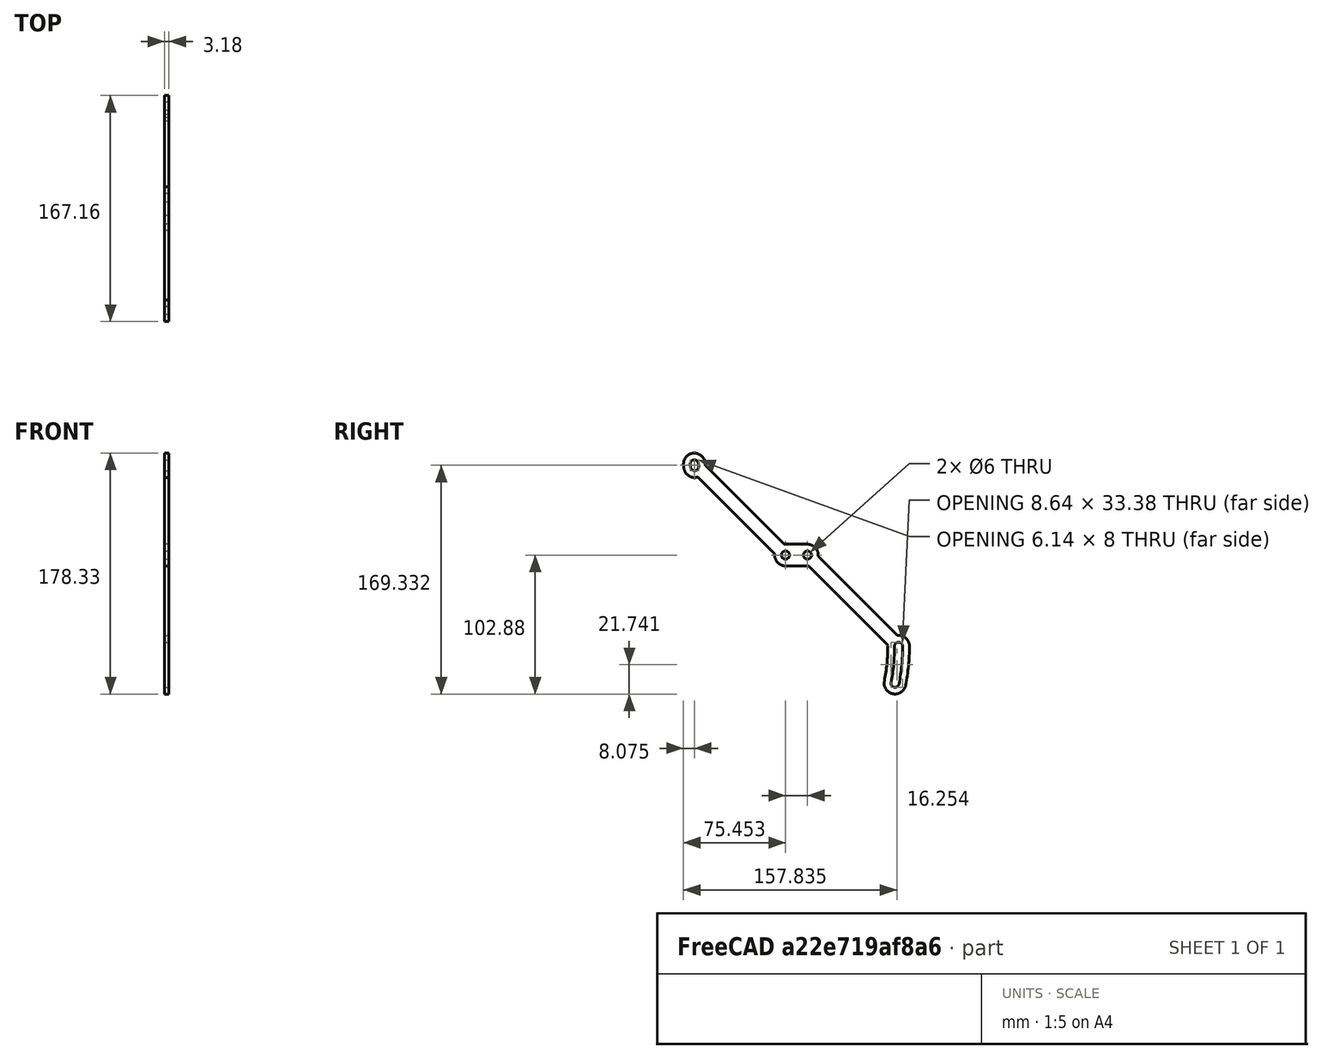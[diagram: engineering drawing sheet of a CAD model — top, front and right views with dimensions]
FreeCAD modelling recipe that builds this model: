
FCSTD DOCUMENT  (FreeCAD 1.0R38641 +468 (Git))
Label: frame_bracket
License: All rights reserved
LicenseURL: https://en.wikipedia.org/wiki/All_rights_reserved
objects: PartDesign::SubShapeBinder×1, Sketcher::SketchObject×1, PartDesign::Pad×1, PartDesign::Body×1
note: 7 computed .brp shape members not serialized (recipe doc carries the construction recipe); baked Part::Feature solids carry a one-line shape summary decoded from their .brp
EXTERNAL_REF file=panel_side.FCStd obj=Body001
EXTERNAL_REF file=dimensions.FCStd obj=VarSet

FEATURE [PartDesign::SubShapeBinder] Binder  label="SidePanelBinder"
  BindCopyOnChange = 0
  BindMode = 0
  ClaimChildren = false
  Context = -> Body [Binder.]
  Fuse = false
  MakeFace = true
  OffsetFill = false
  OffsetIntersection = false
  OffsetJoinType = 0
  OffsetOpenResult = false
  PartialLoad = false
  Refine = true
  Relative = true
  Support = -> [<external panel_side.FCStd>#Body001]
  _Version = 2
FEATURE [Sketcher::SketchObject] Sketch
  ArcFitTolerance = 1e-06
  AttachmentSupport = -> [Binder]
  ExternalGeometry = -> [Binder]
  FullyConstrained = true
  MakeInternals = false
  MapMode = 5
  Placement = pos=(-1.8542,0,0) rot=(0.57735,0.57735,0.57735;2.0944rad)
  expr: Constraints[114] = dimensions#VarSet.MaxAngle / 2
  expr: Constraints[115] = dimensions#VarSet.MaxAngle / 2
  expr: Constraints[63] = dimensions#VarSet.FrameHoleDiameter
  sketch-geometry (47):
    g0: Circle CenterX=56.923 CenterY=-56.25 CenterZ=0 NormalX=0 NormalY=0 NormalZ=1 AngleXU=0 Radius=3
    g1: Circle CenterX=73.177 CenterY=-56.25 CenterZ=0 NormalX=0 NormalY=0 NormalZ=1 AngleXU=0 Radius=3
    g2: ArcOfCircle CenterX=56.923 CenterY=-56.25 CenterZ=0 NormalX=0 NormalY=0 NormalZ=1 AngleXU=0 Radius=8 StartAngle=3.09569 EndAngle=4.71239
    g3: ArcOfCircle CenterX=73.177 CenterY=-56.25 CenterZ=0 NormalX=0 NormalY=0 NormalZ=1 AngleXU=0 Radius=8 StartAngle=6.23728 EndAngle=7.85398
    g4: ArcOfCircle CenterX=4.7e-14 CenterY=11.2 CenterZ=0 NormalX=0 NormalY=0 NormalZ=1 AngleXU=0 Radius=18.527 StartAngle=3.14159 EndAngle=3.33794
    g5: ArcOfCircle CenterX=-10.527 CenterY=11.2 CenterZ=0 NormalX=0 NormalY=0 NormalZ=1 AngleXU=0 Radius=8 StartAngle=6.23728 EndAngle=9.42478
    g6: ArcOfCircle CenterX=4.7e-14 CenterY=11.2 CenterZ=0 NormalX=0 NormalY=0 NormalZ=1 AngleXU=0 Radius=13.527 StartAngle=3.14159 EndAngle=3.33794
    g7: ArcOfCircle CenterX=-10.3247 CenterY=9.14628 CenterZ=0 NormalX=0 NormalY=0 NormalZ=1 AngleXU=0 Radius=3 StartAngle=3.33794 EndAngle=6.47953
    g8: ArcOfCircle CenterX=-10.527 CenterY=11.2 CenterZ=0 NormalX=0 NormalY=0 NormalZ=1 AngleXU=0 Radius=3 StartAngle=0 EndAngle=3.14159
    g9: ArcOfCircle CenterX=4.7e-14 CenterY=11.2 CenterZ=0 NormalX=0 NormalY=0 NormalZ=1 AngleXU=0 Radius=7.527 StartAngle=3.14159 EndAngle=3.33794
    g10: ArcOfCircle CenterX=4.67e-14 CenterY=-123.7 CenterZ=0 NormalX=0 NormalY=0 NormalZ=1 AngleXU=0 Radius=148.627 StartAngle=6.08684 EndAngle=6.28319
    g11: ArcOfCircle CenterX=137.925 CenterY=-151.135 CenterZ=0 NormalX=0 NormalY=0 NormalZ=1 AngleXU=0 Radius=8 StartAngle=2.94524 EndAngle=6.08684
    g12: ArcOfCircle CenterX=4.67e-14 CenterY=-123.7 CenterZ=0 NormalX=0 NormalY=0 NormalZ=1 AngleXU=0 Radius=132.627 StartAngle=6.08684 EndAngle=6.28648
    g13: ArcOfCircle CenterX=4.67e-14 CenterY=-123.7 CenterZ=0 NormalX=0 NormalY=0 NormalZ=1 AngleXU=0 Radius=143.627 StartAngle=6.08684 EndAngle=6.28319
    g14: ArcOfCircle CenterX=140.627 CenterY=-123.7 CenterZ=0 NormalX=0 NormalY=0 NormalZ=1 AngleXU=0 Radius=3 StartAngle=3e-16 EndAngle=3.14159
    g15: ArcOfCircle CenterX=137.925 CenterY=-151.135 CenterZ=0 NormalX=0 NormalY=0 NormalZ=1 AngleXU=0 Radius=3 StartAngle=2.94524 EndAngle=6.08684
    g16: ArcOfCircle CenterX=4.67e-14 CenterY=-123.7 CenterZ=0 NormalX=0 NormalY=0 NormalZ=1 AngleXU=0 Radius=137.627 StartAngle=6.08684 EndAngle=6.28319
    g17: LineSegment [constr] StartX=4.67e-14 StartY=-123.7 StartZ=0 EndX=148.627 EndY=-123.7 EndZ=0
    g18: LineSegment [constr] StartX=4.7e-14 StartY=11.2 StartZ=0 EndX=-18.527 EndY=11.2 EndZ=0
    g19: LineSegment [constr] StartX=56.923 StartY=-56.25 StartZ=0 EndX=-10.527 EndY=11.2 EndZ=0
    g20: LineSegment [constr] StartX=73.177 StartY=-56.25 StartZ=0 EndX=140.627 EndY=-123.7 EndZ=0
    g21: LineSegment [constr] StartX=73.177 StartY=-59.25 StartZ=0 EndX=76.177 EndY=-59.25 EndZ=0
    g22: LineSegment StartX=81.5188 StartY=-57.5207 StartZ=0 EndX=139.356 EndY=-115.358 EndZ=0
    g23: LineSegment StartX=74.4574 StartY=-64.6015 StartZ=0 EndX=132.275 EndY=-122.419 EndZ=0
    g24: LineSegment StartX=-7.42456 StartY=1.02649 StartZ=0 EndX=48.5812 EndY=-54.9793 EndZ=0
    g25: LineSegment StartX=55.6426 StartY=-47.8985 StartZ=0 EndX=-2.18522 EndY=9.92929 EndZ=0
    g26: ArcOfCircle CenterX=47.7327 CenterY=-55.8278 CenterZ=0 NormalX=0 NormalY=0 NormalZ=1 AngleXU=0 Radius=1.2 StartAngle=6.23728 EndAngle=7.06858
    g27: LineSegment StartX=56.4911 StartY=-48.25 StartZ=0 EndX=73.177 EndY=-48.25 EndZ=0
    g28: ArcOfCircle CenterX=56.4911 CenterY=-47.05 CenterZ=0 NormalX=0 NormalY=0 NormalZ=1 AngleXU=0 Radius=1.2 StartAngle=3.92699 EndAngle=4.71239
    g29: ArcOfCircle CenterX=82.3673 CenterY=-56.6722 CenterZ=0 NormalX=0 NormalY=0 NormalZ=1 AngleXU=0 Radius=1.2 StartAngle=3.09569 EndAngle=3.92699
    g30: ArcOfCircle CenterX=73.6089 CenterY=-65.45 CenterZ=0 NormalX=0 NormalY=0 NormalZ=1 AngleXU=0 Radius=1.2 StartAngle=0.785398 EndAngle=1.5708
    g31: LineSegment StartX=56.923 StartY=-64.25 StartZ=0 EndX=73.6089 EndY=-64.25 EndZ=0
    g32: ArcOfCircle CenterX=140.627 CenterY=-123.7 CenterZ=0 NormalX=0 NormalY=0 NormalZ=1 AngleXU=0 Radius=8 StartAngle=2e-16 EndAngle=1.6167
    g33: ArcOfCircle CenterX=140.205 CenterY=-114.51 CenterZ=0 NormalX=0 NormalY=0 NormalZ=1 AngleXU=0 Radius=1.2 StartAngle=3.92699 EndAngle=4.75829
    g34: ArcOfCircle CenterX=131.426 CenterY=-123.267 CenterZ=0 NormalX=0 NormalY=0 NormalZ=1 AngleXU=0 Radius=1.2 StartAngle=0.00329147 EndAngle=0.785398
    g35: ArcOfCircle CenterX=-10.3247 CenterY=9.14628 CenterZ=0 NormalX=0 NormalY=0 NormalZ=1 AngleXU=0 Radius=8 StartAngle=3.33794 EndAngle=4.93728
    g36: ArcOfCircle CenterX=-8.27309 CenterY=0.177963 CenterZ=0 NormalX=0 NormalY=0 NormalZ=1 AngleXU=0 Radius=1.2 StartAngle=0.785398 EndAngle=1.79569
    g37: ArcOfCircle CenterX=-1.33669 CenterY=10.7778 CenterZ=0 NormalX=0 NormalY=0 NormalZ=1 AngleXU=0 Radius=1.2 StartAngle=3.09569 EndAngle=3.92699
    g38: LineSegment [constr] StartX=4.7e-14 StartY=11.2 StartZ=0 EndX=4.7e-14 EndY=10 EndZ=0
    g39: LineSegment [constr] StartX=4.67e-14 StartY=-123.7 StartZ=0 EndX=4.67e-14 EndY=-122.5 EndZ=0
    g40: LineSegment [constr] StartX=53.923 StartY=-53.25 StartZ=0 EndX=56.923 EndY=-53.25 EndZ=0
    g41: LineSegment [constr] StartX=56.923 StartY=-53.25 StartZ=0 EndX=56.923 EndY=-56.25 EndZ=0
    g42: LineSegment [constr] StartX=73.177 StartY=-56.25 StartZ=0 EndX=73.177 EndY=-59.25 EndZ=0
    g43: LineSegment [constr] StartX=103.366 StartY=-93.5105 StartZ=0 EndX=106.902 EndY=-89.975 EndZ=0
    g44: LineSegment [constr] StartX=106.902 StartY=-89.975 StartZ=0 EndX=110.438 EndY=-86.4395 EndZ=0
    g45: LineSegment [constr] StartX=19.6625 StartY=-26.0605 StartZ=0 EndX=23.198 EndY=-22.525 EndZ=0
    g46: LineSegment [constr] StartX=23.198 StartY=-22.525 StartZ=0 EndX=26.7335 EndY=-18.9895 EndZ=0
  constraints (116):
    c: Coincident(g2,g0)
    c: Coincident(g3,g1)
    c: Tangent(g4,g5) = -1.5708
    c: Tangent(g4,g35) = -1.5708
    c: Coincident(g6,g9)
    c: Tangent(g9,g8) = 1.5708
    c: Tangent(g9,g7) = 1.5708
    c: Tangent(g6,g8) = -1.5708
    c: Tangent(g6,g7) = -1.5708
    c: Coincident(g6,g4)
    c: Coincident(g7,g35)
    c: Coincident(g10,g12)
    c: Tangent(g12,g11) = 1.5708
    c: Tangent(g10,g32) = -1.5708
    c: Tangent(g10,g11) = -1.5708
    c: Coincident(g13,g16)
    c: Tangent(g16,g15) = 1.5708
    c: Tangent(g16,g14) = 1.5708
    c: Tangent(g13,g15) = -1.5708
    c: Tangent(g13,g14) = -1.5708
    c: Coincident(g13,g10)
    c: Coincident(g14,g32)
    c: Coincident(g17,g10)
    c: Equal(g0,g1)
    c: Equal(g1,g14)
    c: Equal(g7,g0)
    c: Coincident(g18,g4)
    c: Horizontal(g18)
    c: Coincident(g4,g18)
    c: Coincident(g19,g0)
    c: Coincident(g5,g19)
    c: Coincident(g20,g1)
    c: PointOnObject(g21,g1)
    c: PointOnObject(g21,g20)
    c: Horizontal(g21)
    c: Coincident(g20,g32)
    c: Parallel(g23,g20)
    c: Parallel(g20,g22)
    c: Parallel(g24,g19)
    c: Parallel(g19,g25)
    c: Tangent(g26,g2) = 1.5708
    c: Tangent(g24,g26) = 1.5708
    c: Horizontal(g27)
    c: Tangent(g28,g27) = -1.5708
    c: Tangent(g25,g28) = 1.5708
    c: Tangent(g29,g3) = 1.5708
    c: Tangent(g29,g22) = -1.5708
    c: Tangent(g23,g30) = 1.5708
    c: Horizontal(g31)
    c: Tangent(g3,g27) = 1.5708
    c: Tangent(g2,g31) = -1.5708
    c: Distance(g25,g24) = 10
    c: Distance(g22,g23) = 10
    c: Tangent(g30,g31) = 1.5708
    c: Tangent(g33,g32) = 1.5708
    c: Tangent(g33,g22) = -1.5708
    c: Tangent(g34,g23) = 1.5708
    c: Coincident(g17,g10)
    c: Tangent(g35,g36) = 1.5708
    c: Tangent(g36,g24) = 1.5708
    c: Tangent(g37,g25) = 1.5708
    c: Coincident(g8,g5)
    c: Tangent(g12,g34) = -1.5708
    c: Diameter(g0) = 6
    c: Coincident(g38,g4)
    c: Coincident(g39,g10)
    c: Horizontal(g17)
    c: Coincident(g15,g11)
    c: Equal(g39,g38)
    c: Distance(g2,g0) = 5
    c: Equal(g2,g3)
    c: Equal(g29,g30)
    c: Equal(g30,g26)
    c: Equal(g28,g26)
    c: Distance(g15,g11) = 5
    c: Distance(g5,g8) = 5
    c: Distance(g38,g38) = 1.2
    c: Tangent(g37,g5) = 1.5708
    c: Equal(g34,g33)
    c: Equal(g33,g30)
    c: PointOnObject(g40,g19)
    c: PointOnObject(g40,g0)
    c: Horizontal(g40)
    c: Coincident(g41,g40)
    c: Coincident(g41,g0)
    c: Vertical(g41)
    c: Equal(g41,g40)
    c: Coincident(g42,g1)
    c: Coincident(g42,g21)
    c: Vertical(g42)
    c: Equal(g42,g21)
    c: Equal(g28,g37)
    c: Equal(g37,g36)
    c: Radius(g30) = 1.2
    c: PointOnObject(g43,g23)
    c: Coincident(g44,g43)
    c: PointOnObject(g44,g22)
    c: Perpendicular(g43,g23)
    c: Perpendicular(g22,g44)
    c: Equal(g43,g44)
    c: PointOnObject(g45,g24)
    c: PointOnObject(g46,g25)
    c: Perpendicular(g25,g46)
    c: Perpendicular(g24,g45)
    c: Coincident(g46,g45)
    c: Equal(g46,g45)
    c: Symmetric(g1,g14,g43)
    c: Symmetric(g0,g5,g45)
    c: Coincident(g1,g-4)
    c: Coincident(g0,g-3)
    c: Coincident(g39,g-5)
    c: Vertical(g39)
    c: Coincident(g38,g-6)
    c: Vertical(g38)
    c: Angle(g10) = 0.19635
    c: Angle(g4) = 0.19635
FEATURE [PartDesign::Pad] Pad
  Direction = (1,0,0)
  Length = 3.175
  Length2 = 10
  Profile = -> Sketch
  ReferenceAxis = -> Sketch [N_Axis]
  Refine = true
  Reversed = true
  Suppressed = false
  Type = 0
  expr: Length = <<dimensions>>#VarSet.FrameTotalThickness
FEATURE [PartDesign::Body] Body  label="FrameBracket"
  AllowCompound = false
  Group = -> [Sketch,Pad,Binder]
  Origin = -> Origin
  Tip = -> Pad
